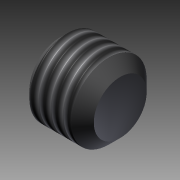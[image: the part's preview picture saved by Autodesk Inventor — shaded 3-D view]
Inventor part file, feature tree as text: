
AUTODESK INVENTOR PART (.ipt)
format: ipt  version: 2011 SP1 (Build 150282100, 282)  size: 114,688 bytes
history: native  units: mm
features: other x7, sketch x3, revolve x2, thread x1, extrude x1
ambient origin geometry x8: Origin, YZ Plane, XZ Plane, XY Plane, X Axis, Y Axis, Z Axis, Center Point
bodies: Solid1 (feature_tree)
feature tree (14):
  revolve  "Revolution1"  [1 undecoded]
  thread  "Thread1"  [1 undecoded]
  extrude  "Extrusion1"  TaperAngle=0.0deg  [1 undecoded]
  revolve  "Revolution2"  [1 undecoded]
  other  "CP_XY"
  other  "CP_YZ"
  other  "CP_ZX"
  other  "CP_X"
  other  "CP_Y"
  other  "CP_Z"
  other  "CP_Center"
  sketch  "Sketch_1"  dims[d0=360.0deg d1=2.7595mm d2=0.0mm d3=2.0mm d4=0.0mm]
  sketch  "Sketch_2"  dims[d5=360.0deg d6=0.0mm]
  sketch  "Sketch_3"
note: 4 required parameter values undecoded (feature->parameter linkage not recoverable at this tier; creation-order binding heuristic only, values carry confidence <= 0.55)